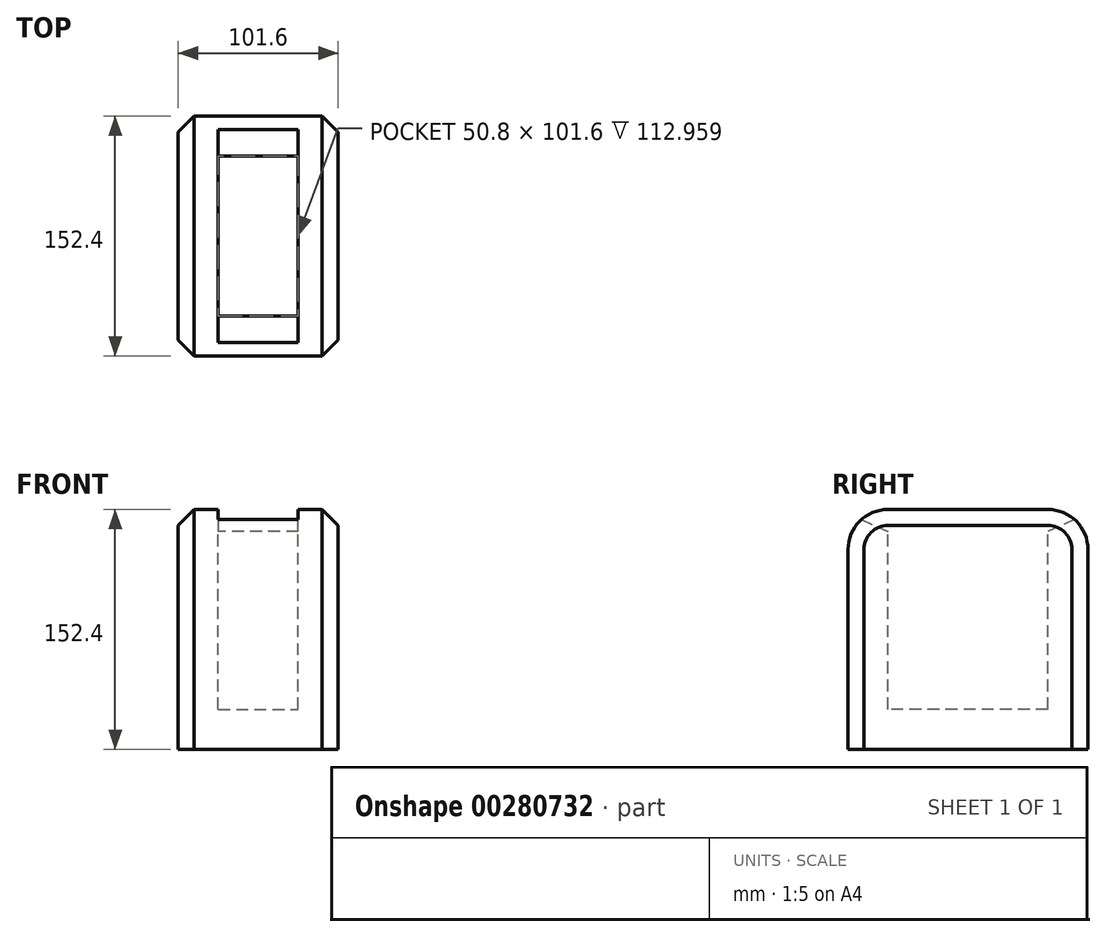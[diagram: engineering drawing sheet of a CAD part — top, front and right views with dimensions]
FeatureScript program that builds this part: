
annotation { "Feature Type Name" : "Feature", "Feature Type Description" : "" }
export const myFeature = defineFeature(function(context is Context, id is Id, definition is map)
    precondition{}
    {
        {
            var Q0;
            Q0=qCreatedBy(makeId("Top.planeOp"),FACE);
            var sketch = newSketch(context, id + "F0", { "sketchPlane" : qUnion([Q0])});
            skLineSegment(sketch, "E0.bottom", {"start": v(-1.58, -2.21) * mm, "end": v(100.02, -2.21) * mm});
            skLineSegment(sketch, "E0.top", {"start": v(-1.58, 150.19) * mm, "end": v(100.02, 150.19) * mm});
            skLineSegment(sketch, "E0.left", {"start": v(-1.58, -2.21) * mm, "end": v(-1.58, 150.19) * mm});
            skLineSegment(sketch, "E0.right", {"start": v(100.02, -2.21) * mm, "end": v(100.02, 150.19) * mm});
            skSolve(sketch);
        }
        {
            var Q0;
            Q0=makeQuery(id+"F0.imprint","IMPRINT",FACE,{"disambiguationData":[TD([[makeQuery(id+"F0.imprint","IMPRINT",EDGE,{"derivedFrom":sQuery(id+"F0.wireOp",EDGE,"E0.bottom")}),1.0]])]});
            extrude(context, id + "F1", {"entities" : qUnion([Q0]), "depth" : 152.4 * mm});
        }
        {
            var Q0;
            Q0=makeQuery(id+"F1.opExtrude","CAP_FACE",FACE,{"disambiguationData":[OSD([sQuery(id+"F0.wireOp",EDGE,"E0.bottom"),sQuery(id+"F0.wireOp",EDGE,"E0.top"),sQuery(id+"F0.wireOp",EDGE,"E0.left"),sQuery(id+"F0.wireOp",EDGE,"E0.right")])],"isStart":false});
            var sketch = newSketch(context, id + "F2", { "sketchPlane" : qUnion([Q0])});
            skLineSegment(sketch, "E1.bottom", {"start": v(23.82, 124.79) * mm, "end": v(74.62, 124.79) * mm});
            skLineSegment(sketch, "E1.top", {"start": v(23.82, 23.19) * mm, "end": v(74.62, 23.19) * mm});
            skLineSegment(sketch, "E1.left", {"start": v(23.82, 124.79) * mm, "end": v(23.82, 23.19) * mm});
            skLineSegment(sketch, "E1.right", {"start": v(74.62, 124.79) * mm, "end": v(74.62, 23.19) * mm});
            skSolve(sketch);
        }
        {
            var Q0;
            Q0=makeQuery(id+"F2.imprint","IMPRINT",FACE,{"disambiguationData":[TD([[makeQuery(id+"F2.imprint","IMPRINT",EDGE,{"derivedFrom":sQuery(id+"F2.wireOp",EDGE,"E1.bottom")}),-1.0]])]});
            extrude(context, id + "F3", {"entities" : qUnion([Q0]), "operationType" : NewBodyOperationType.REMOVE, "oppositeDirection" : true, "depth" : 127 * mm});
        }
        {
            var Q0;
            Q0=makeQuery(id+"F1.opExtrude","CAP_EDGE",EDGE,{"disambiguationData":[OSD([sQuery(id+"F0.wireOp",EDGE,"E0.bottom")])],"isStart":false});
            var Q1;
            Q1=makeQuery(id+"F1.opExtrude","CAP_EDGE",EDGE,{"disambiguationData":[OSD([sQuery(id+"F0.wireOp",EDGE,"E0.top")])],"isStart":false});
            fillet(context, id + "F4", {"entities" : qUnion([Q0, Q1]), "radius" : 25.4 * mm, "tangentPropagation" : true, "allowEdgeOverflow" : false});
        }
        {
            var Q0;
            Q0=makeQuery(id+"F4.opFillet","BLEND_EDGE",EDGE,{"blendedFrom":[makeQuery(id+"F1.opExtrude","CAP_EDGE",EDGE,{"disambiguationData":[OSD([sQuery(id+"F0.wireOp",EDGE,"E0.bottom")])],"isStart":false}),makeQuery(id+"F1.opExtrude","SWEPT_FACE",FACE,{"disambiguationData":[OSD([sQuery(id+"F0.wireOp",EDGE,"E0.right")])]})],"blendedInto":[makeQuery(id+"F1.opExtrude","SWEPT_FACE",FACE,{"disambiguationData":[OSD([sQuery(id+"F0.wireOp",EDGE,"E0.right")])]})]});
            var Q1;
            Q1=makeQuery(id+"F4.opFillet","BLEND_EDGE",EDGE,{"blendedFrom":[makeQuery(id+"F1.opExtrude","CAP_EDGE",EDGE,{"disambiguationData":[OSD([sQuery(id+"F0.wireOp",EDGE,"E0.bottom")])],"isStart":false}),makeQuery(id+"F1.opExtrude","SWEPT_FACE",FACE,{"disambiguationData":[OSD([sQuery(id+"F0.wireOp",EDGE,"E0.left")])]})],"blendedInto":[makeQuery(id+"F1.opExtrude","SWEPT_FACE",FACE,{"disambiguationData":[OSD([sQuery(id+"F0.wireOp",EDGE,"E0.left")])]})]});
            var Q2;
            Q2=makeQuery(id+"F3.boolean.opBoolean","COPY",EDGE,{"derivedFrom":makeQuery(id+"F3.opExtrude","CAP_EDGE",EDGE,{"disambiguationData":[OSD([sQuery(id+"F2.wireOp",EDGE,"E1.left")])],"isStart":true})});
            var Q3;
            Q3=makeQuery(id+"F4.opFillet","BLEND_EDGE",EDGE,{"blendedFrom":[makeQuery(id+"F1.opExtrude","CAP_EDGE",EDGE,{"disambiguationData":[OSD([sQuery(id+"F0.wireOp",EDGE,"E0.top")])],"isStart":false}),makeQuery(id+"F3.boolean.opBoolean","COPY",FACE,{"derivedFrom":makeQuery(id+"F3.opExtrude","SWEPT_FACE",FACE,{"disambiguationData":[OSD([sQuery(id+"F2.wireOp",EDGE,"E1.bottom")])]})})],"blendedInto":[makeQuery(id+"F3.boolean.opBoolean","COPY",FACE,{"derivedFrom":makeQuery(id+"F3.opExtrude","SWEPT_FACE",FACE,{"disambiguationData":[OSD([sQuery(id+"F2.wireOp",EDGE,"E1.bottom")])]})})]});
            var Q4;
            Q4=makeQuery(id+"F3.boolean.opBoolean","COPY",EDGE,{"derivedFrom":makeQuery(id+"F3.opExtrude","CAP_EDGE",EDGE,{"disambiguationData":[OSD([sQuery(id+"F2.wireOp",EDGE,"E1.right")])],"isStart":true})});
            var Q5;
            Q5=makeQuery(id+"F4.opFillet","BLEND_EDGE",EDGE,{"blendedFrom":[makeQuery(id+"F1.opExtrude","CAP_EDGE",EDGE,{"disambiguationData":[OSD([sQuery(id+"F0.wireOp",EDGE,"E0.bottom")])],"isStart":false}),makeQuery(id+"F3.boolean.opBoolean","COPY",FACE,{"derivedFrom":makeQuery(id+"F3.opExtrude","SWEPT_FACE",FACE,{"disambiguationData":[OSD([sQuery(id+"F2.wireOp",EDGE,"E1.top")])]})})],"blendedInto":[makeQuery(id+"F3.boolean.opBoolean","COPY",FACE,{"derivedFrom":makeQuery(id+"F3.opExtrude","SWEPT_FACE",FACE,{"disambiguationData":[OSD([sQuery(id+"F2.wireOp",EDGE,"E1.top")])]})})]});
            chamfer(context, id + "F5", {"entities" : qUnion([Q0, Q1, Q2, Q3, Q4, Q5]), "width" : 10.16 * mm, "tangentPropagation" : true});
        }
    });
